# Revit family: TREND_215x145x2
name_source: partatom
category: Plumbing Fixtures
revit_build: Autodesk Revit 2018 (Build: 20170223_1515(x64)
units: mm (PartAtom-declared; Revit-internal decimal feet)

## family parameters
Always vertical = Yes
Cut with Voids When Loaded = No
OmniClass Number = 23.45.00.00
OmniClass Title = Sanitary, Laundry, and Cleaning Equipment
Part Type = Normal
Room Calculation Point = No
Round Connector Dimension = Use Diameter
Shared = No
Work Plane-Based = Yes

## types (2) — shared parameters
BIM object developer = www.concepsysbim.com
CONTROL_Brief description = Plaque de commande en inox chromé
CONTROL_Installation instructions = http://www.oli-world.com
CONTROL_Model = TREND
CONTROL_Product data url = https://www.regiplast.fr
CONTROL_Type of flush = Double-Débit
CONTROL_Type/function = Plaque de Commande pour réservoir à encastrer
CONTROL_Vandal-proof = Oui
Default Elevation = 1219.2 mm  [stored 4 ft]
Description = Plaque de commande en inox chromé
HORIZONTAL = No
Model = TREND
Product data url = https://www.regiplast.fr
URL = https://www.regiplast.fr
VERTICAL = Yes

## per-type parameters (varying)
| type | CONTROL_Actuation type | CONTROL_Height | CONTROL_Length | CONTROL_Material | CONTROL_Model Series | CONTROL_Model code/ref | CONTROL_Width |
| Pneumatique_Inox chromé | Pneumatique | 145 mm  [stored 0.475722 ft] | 215 mm | Inox brossé | Inox chromé | 1626IC | 2 mm  [stored 0.00656168 ft] |
| Mécanique_Inox Brossé | Mécanique | 163 mm  [stored 0.534777 ft] | 243 mm | Zamac chromée Mate | Inox Brossé | 1626IB | 17 mm |

note: [stored X ft] marks values corroborated as IEEE doubles in the binary element streams (Revit-internal decimal feet)

## geometry (parser evidence)
native form markers: Sweep x7
no freeform markers — native parametric forms only
